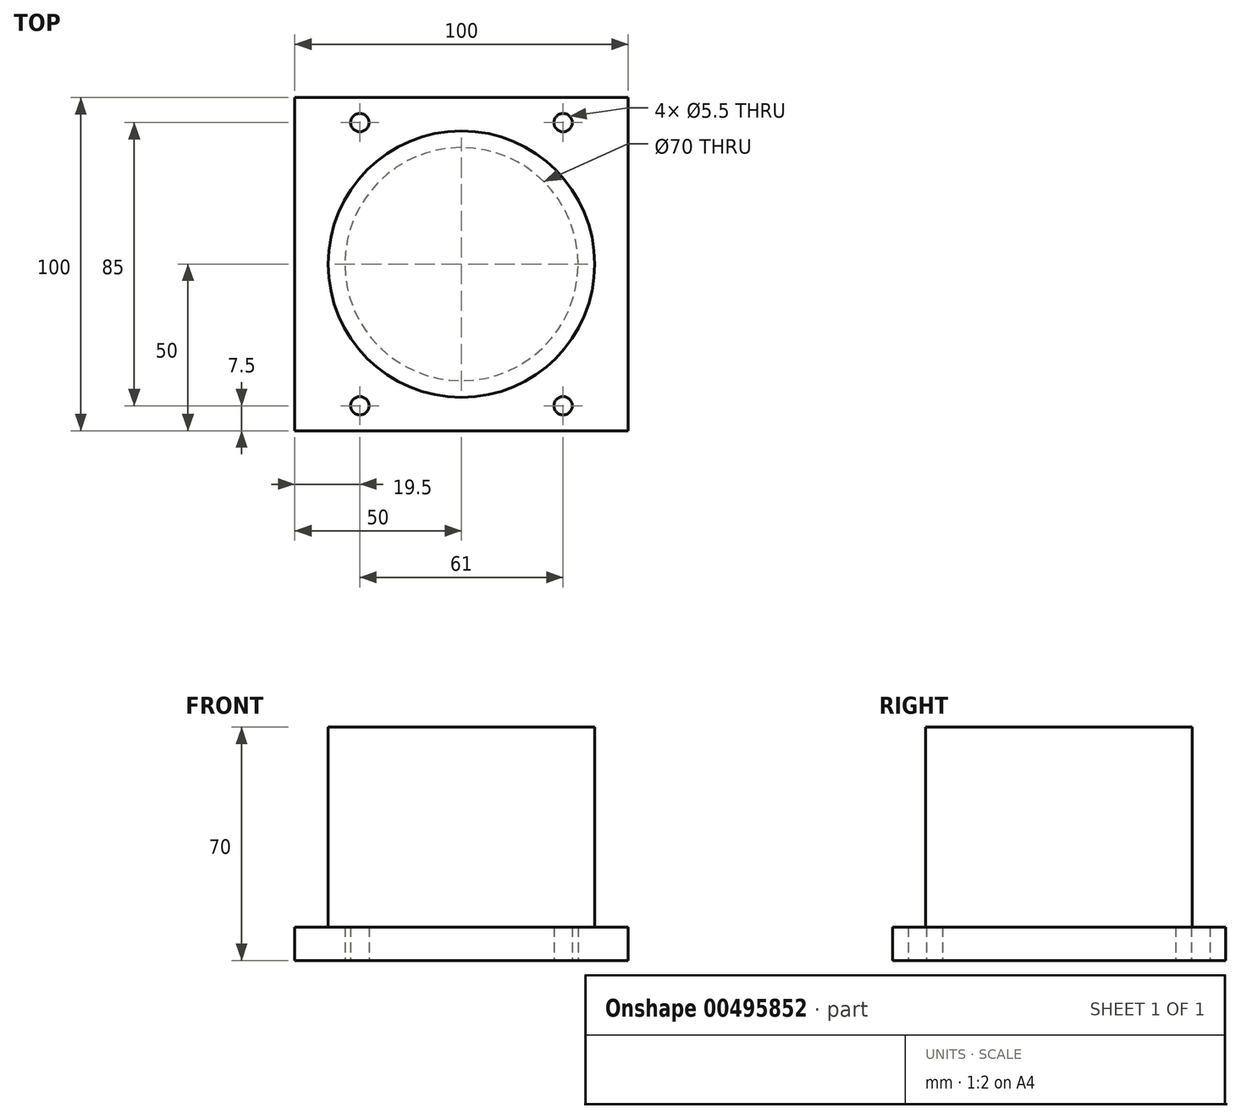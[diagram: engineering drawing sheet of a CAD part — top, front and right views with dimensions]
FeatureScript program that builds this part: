
annotation { "Feature Type Name" : "Feature", "Feature Type Description" : "" }
export const myFeature = defineFeature(function(context is Context, id is Id, definition is map)
    precondition{}
    {
        {
            var Q0;
            Q0=qCreatedBy(makeId("Top.planeOp"),FACE);
            var sketch = newSketch(context, id + "F0", { "sketchPlane" : qUnion([Q0])});
            skLineSegment(sketch, "E0.bottom", {"start": v(-50, -50) * mm, "end": v(50, -50) * mm});
            skLineSegment(sketch, "E0.top", {"start": v(-50, 50) * mm, "end": v(50, 50) * mm});
            skLineSegment(sketch, "E0.left", {"start": v(-50, -50) * mm, "end": v(-50, 50) * mm});
            skLineSegment(sketch, "E0.right", {"start": v(50, -50) * mm, "end": v(50, 50) * mm});
            skPoint(sketch, "E0.middle", {"position": v(0, 0) * mm});
            skCircle(sketch, "E1", {"center": v(-30.5, 42.5) * mm, "radius": 2.75 * mm});
            skCircle(sketch, "E2", {"center": v(30.5, 42.5) * mm, "radius": 2.75 * mm});
            skCircle(sketch, "E3", {"center": v(-30.5, -42.5) * mm, "radius": 2.75 * mm});
            skCircle(sketch, "E4", {"center": v(30.5, -42.5) * mm, "radius": 2.75 * mm});
            skCircle(sketch, "E5", {"center": v(0, 0) * mm, "radius": 35 * mm});
            skSolve(sketch);
        }
        {
            var Q0;
            Q0=makeQuery(id+"F0.imprint","IMPRINT",FACE,{"disambiguationData":[TD([[makeQuery(id+"F0.imprint","IMPRINT",EDGE,{"derivedFrom":sQuery(id+"F0.wireOp",EDGE,"E0.bottom")}),1.0]])]});
            extrude(context, id + "F1", {"entities" : qUnion([Q0]), "depth" : 10 * mm});
        }
        {
            var Q0;
            Q0=makeQuery(id+"F1.opExtrude","CAP_FACE",FACE,{"disambiguationData":[OSD([sQuery(id+"F0.wireOp",EDGE,"E0.bottom"),sQuery(id+"F0.wireOp",EDGE,"E0.top"),sQuery(id+"F0.wireOp",EDGE,"E0.left"),sQuery(id+"F0.wireOp",EDGE,"E0.right"),sQuery(id+"F0.wireOp",EDGE,"E1"),sQuery(id+"F0.wireOp",EDGE,"E2"),sQuery(id+"F0.wireOp",EDGE,"E3"),sQuery(id+"F0.wireOp",EDGE,"E4"),sQuery(id+"F0.wireOp",EDGE,"E5")])],"isStart":false});
            var sketch = newSketch(context, id + "F2", { "sketchPlane" : qUnion([Q0])});
            skCircle(sketch, "E6", {"center": v(0, 0) * mm, "radius": 40 * mm});
            skSolve(sketch);
        }
        {
            var Q0;
            Q0=makeQuery(id+"F2.imprint","IMPRINT",FACE,{"disambiguationData":[TD([[makeQuery(id+"F2.imprint","IMPRINT",EDGE,{"derivedFrom":sQuery(id+"F2.wireOp",EDGE,"E6")}),1.0]])]});
            var Q1;
            Q1=makeQuery(id+"F2.imprint","IMPRINT",FACE,{"disambiguationData":[TD([[makeQuery(id+"F2.imprint","IMPRINT",EDGE,{"derivedFrom":makeQuery(id+"F1.opExtrude","CAP_EDGE",EDGE,{"disambiguationData":[OSD([sQuery(id+"F0.wireOp",EDGE,"E5")])],"isStart":false})}),1.0]])]});
            extrude(context, id + "F3", {"entities" : qUnion([Q0, Q1]), "depth" : 60 * mm});
        }
    });
